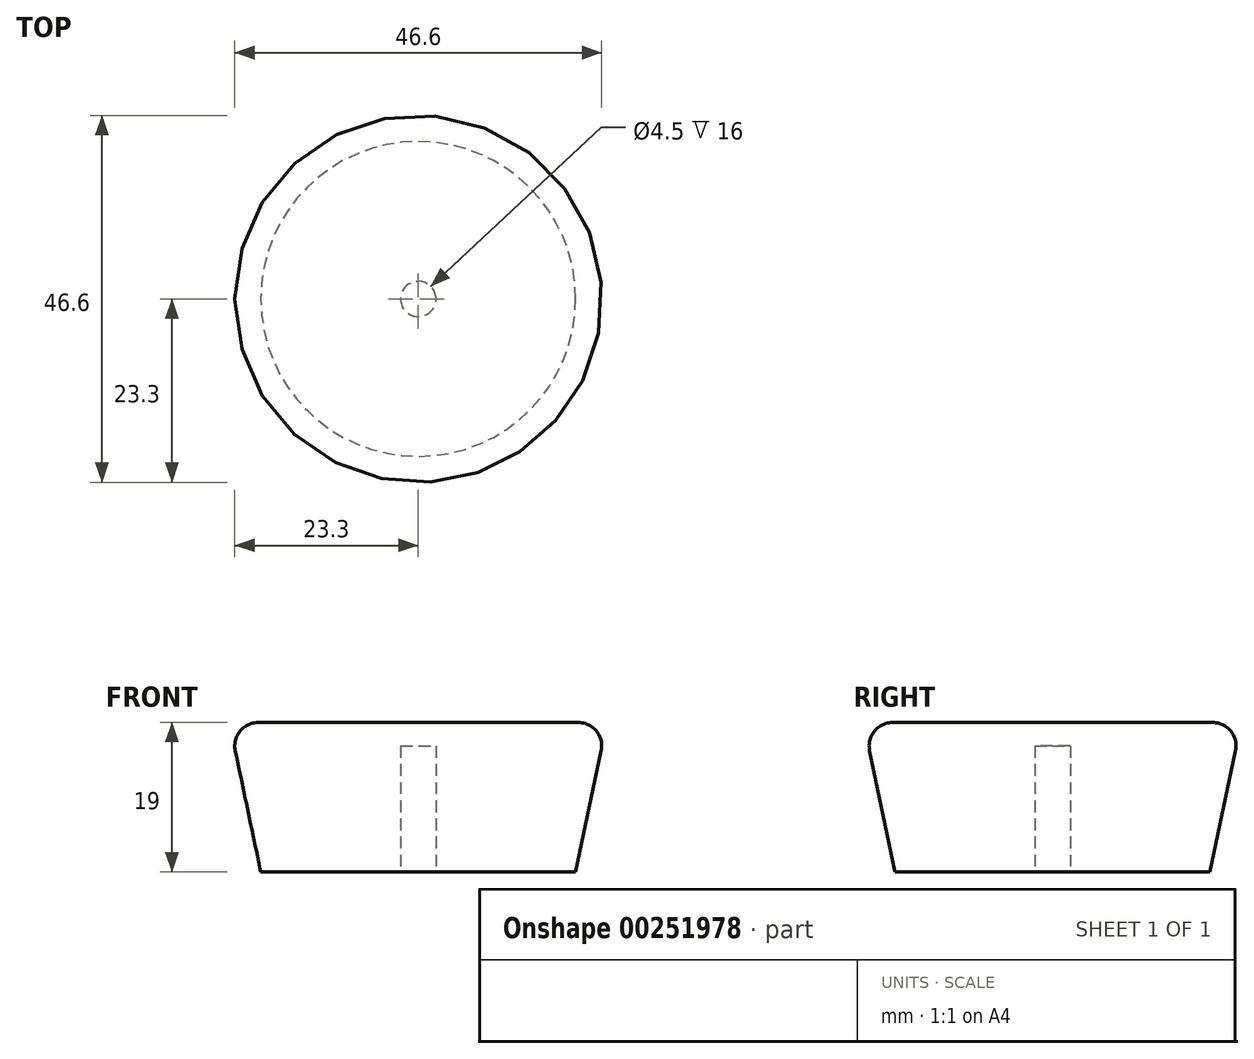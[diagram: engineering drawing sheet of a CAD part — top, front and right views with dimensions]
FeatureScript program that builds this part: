
annotation { "Feature Type Name" : "Feature", "Feature Type Description" : "" }
export const myFeature = defineFeature(function(context is Context, id is Id, definition is map)
    precondition{}
    {
        {
            var Q0;
            Q0=qCreatedBy(makeId("Front.planeOp"),FACE);
            var sketch = newSketch(context, id + "F0", { "sketchPlane" : qUnion([Q0])});
            skLineSegment(sketch, "E0", {"start": v(0, 0) * mm, "end": v(0, 19) * mm});
            skLineSegment(sketch, "E1", {"start": v(0, 19) * mm, "end": v(24, 19) * mm});
            skLineSegment(sketch, "E2", {"start": v(24, 19) * mm, "end": v(20, 0) * mm});
            skLineSegment(sketch, "E3", {"start": v(20, 0) * mm, "end": v(0, 0) * mm});
            skSolve(sketch);
        }
        {
            var Q0;
            Q0 = qSketchRegion(id + "F0", true);
            var Q1;
            Q1=sQuery(id+"F0.wireOp",EDGE,"E0");
            revolve(context, id + "F1", {"entities" : qUnion([Q0]), "axis" : qUnion([Q1]), "revolveType" : RevolveType.FULL});
        }
        {
            var Q0;
            Q0=makeQuery(id+"F1.opRevolve","SWEPT_EDGE",EDGE,{"disambiguationData":[OSD([sQuery(id+"F0.wireOp",EDGE,"E1"),sQuery(id+"F0.wireOp",EDGE,"E2")])]});
            fillet(context, id + "F2", {"entities" : qUnion([Q0]), "radius" : 3 * mm, "tangentPropagation" : true, "allowEdgeOverflow" : false});
        }
        {
            var Q0;
            Q0=makeQuery(id+"F1.opRevolve","SWEPT_FACE",FACE,{"disambiguationData":[OSD([sQuery(id+"F0.wireOp",EDGE,"E3")])]});
            var sketch = newSketch(context, id + "F3", { "sketchPlane" : qUnion([Q0])});
            skCircle(sketch, "E4", {"center": v(0, 0) * mm, "radius": 2.25 * mm});
            skSolve(sketch);
        }
        {
            var Q0;
            Q0 = qSketchRegion(id + "F3", true);
            extrude(context, id + "F4", {"entities" : qUnion([Q0]), "operationType" : NewBodyOperationType.REMOVE, "oppositeDirection" : true, "depth" : 16 * mm, "offsetDistance" : 25 * mm});
        }
    });
